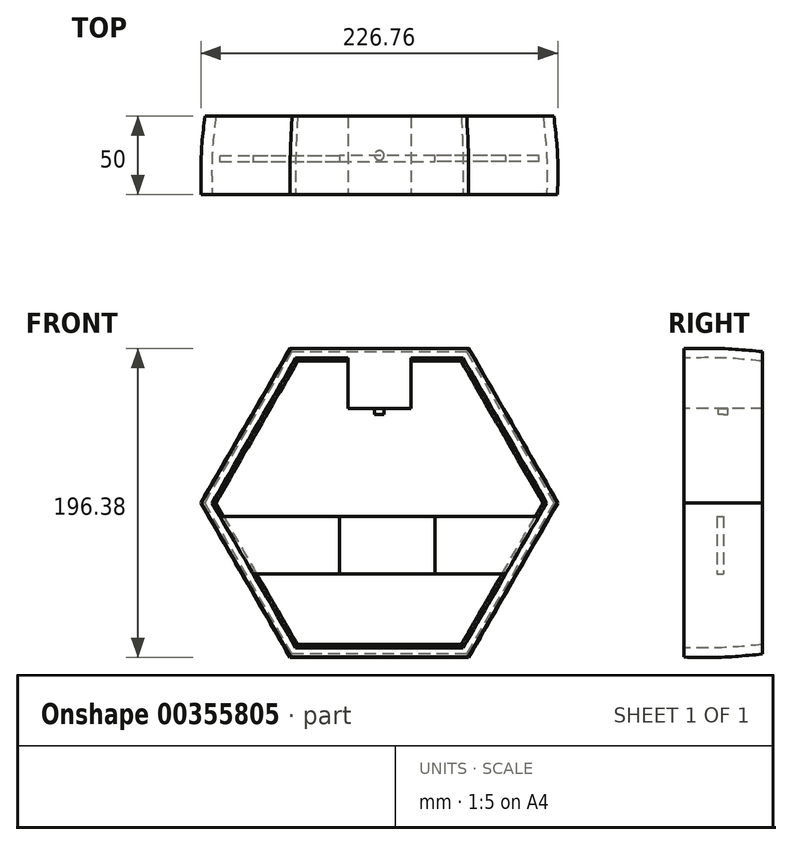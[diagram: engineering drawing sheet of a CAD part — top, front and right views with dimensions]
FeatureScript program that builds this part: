
annotation { "Feature Type Name" : "Feature", "Feature Type Description" : "" }
export const myFeature = defineFeature(function(context is Context, id is Id, definition is map)
    precondition{}
    {
        {
            var Q0;
            Q0=qCreatedBy(makeId("Front.planeOp"),FACE);
            var sketch = newSketch(context, id + "F0", { "sketchPlane" : qUnion([Q0])});
            skCircle(sketch, "E0.cCircle", {"center": v(0, 0) * mm, "radius": 98 * mm, "construction": true});
            skLineSegment(sketch, "E0.0", {"start": v(-56.58, 98) * mm, "end": v(56.58, 98) * mm});
            skLineSegment(sketch, "E0.1", {"start": v(56.58, 98) * mm, "end": v(113.16, 0) * mm});
            skLineSegment(sketch, "E0.2", {"start": v(113.16, 0) * mm, "end": v(56.58, -98) * mm});
            skLineSegment(sketch, "E0.3", {"start": v(56.58, -98) * mm, "end": v(-56.58, -98) * mm});
            skLineSegment(sketch, "E0.4", {"start": v(-56.58, -98) * mm, "end": v(-113.16, 0) * mm});
            skLineSegment(sketch, "E0.5", {"start": v(-113.16, 0) * mm, "end": v(-56.58, 98) * mm});
            skPoint(sketch, "E0.0.midPoint", {"position": v(0, 98) * mm});
            skSolve(sketch);
        }
        {
            var Q0;
            Q0=qCreatedBy(makeId("Front.planeOp"),FACE);
            cPlane(context, id + "F1", {"entities" : qUnion([Q0]), "cplaneType" : CPlaneType.OFFSET, "offset" : 25 * mm, "oppositeDirection" : true, "width" : 150 * mm, "height" : 150 * mm});
        }
        {
            var Q0;
            Q0=qCreatedBy(id+"F1.planeOp",FACE);
            var sketch = newSketch(context, id + "F2", { "sketchPlane" : qUnion([Q0])});
            skCircle(sketch, "E1.cCircle", {"center": v(0, 0) * mm, "radius": 96 * mm, "construction": true});
            skLineSegment(sketch, "E1.0", {"start": v(-55.43, 96) * mm, "end": v(55.43, 96) * mm});
            skLineSegment(sketch, "E1.1", {"start": v(55.43, 96) * mm, "end": v(110.85, 0) * mm});
            skLineSegment(sketch, "E1.2", {"start": v(110.85, 0) * mm, "end": v(55.43, -96) * mm});
            skLineSegment(sketch, "E1.3", {"start": v(55.43, -96) * mm, "end": v(-55.43, -96) * mm});
            skLineSegment(sketch, "E1.4", {"start": v(-55.43, -96) * mm, "end": v(-110.85, 0) * mm});
            skLineSegment(sketch, "E1.5", {"start": v(-110.85, 0) * mm, "end": v(-55.43, 96) * mm});
            skPoint(sketch, "E1.0.midPoint", {"position": v(0, 96) * mm});
            skSolve(sketch);
        }
        {
            var Q0;
            Q0=qCreatedBy(makeId("Front.planeOp"),FACE);
            cPlane(context, id + "F3", {"entities" : qUnion([Q0]), "cplaneType" : CPlaneType.OFFSET, "offset" : 25 * mm, "width" : 150 * mm, "height" : 150 * mm});
        }
        {
            var Q0;
            Q0=qCreatedBy(id+"F3.planeOp",FACE);
            var sketch = newSketch(context, id + "F4", { "sketchPlane" : qUnion([Q0])});
            skCircle(sketch, "E2.cCircle", {"center": v(0, 0) * mm, "radius": 98 * mm, "construction": true});
            skLineSegment(sketch, "E2.0", {"start": v(56.58, -98) * mm, "end": v(-56.58, -98) * mm});
            skLineSegment(sketch, "E2.1", {"start": v(-56.58, -98) * mm, "end": v(-113.16, 0) * mm});
            skLineSegment(sketch, "E2.2", {"start": v(-113.16, 0) * mm, "end": v(-56.58, 98) * mm});
            skLineSegment(sketch, "E2.3", {"start": v(-56.58, 98) * mm, "end": v(56.58, 98) * mm});
            skLineSegment(sketch, "E2.4", {"start": v(56.58, 98) * mm, "end": v(113.16, 0) * mm});
            skLineSegment(sketch, "E2.5", {"start": v(113.16, 0) * mm, "end": v(56.58, -98) * mm});
            skPoint(sketch, "E2.0.midPoint", {"position": v(0, -98) * mm});
            skSolve(sketch);
        }
        {
            var Q0;
            Q0=makeQuery(id+"F2.imprint","IMPRINT",FACE,{"disambiguationData":[TD([[makeQuery(id+"F2.imprint","IMPRINT",EDGE,{"derivedFrom":sQuery(id+"F2.wireOp",EDGE,"E1.0")}),-1.0]])]});
            var Q1;
            Q1=makeQuery(id+"F0.imprint","IMPRINT",FACE,{"disambiguationData":[TD([[makeQuery(id+"F0.imprint","IMPRINT",EDGE,{"derivedFrom":sQuery(id+"F0.wireOp",EDGE,"E0.0")}),-1.0]])]});
            var Q2;
            Q2=makeQuery(id+"F4.imprint","IMPRINT",FACE,{"disambiguationData":[TD([[makeQuery(id+"F4.imprint","IMPRINT",EDGE,{"derivedFrom":sQuery(id+"F4.wireOp",EDGE,"E2.0")}),-1.0]])]});
            loft(context, id + "F5", {"sheetProfilesArray" : [{ "sheetProfileEntities" : qUnion([Q0]) }, { "sheetProfileEntities" : qUnion([Q1]) }, { "sheetProfileEntities" : qUnion([Q2]) }]});
        }
        {
            var Q0;
            Q0=makeQuery(id+"F5.opLoft","CAP_FACE",FACE,{"disambiguationData":[OSD([makeQuery(id+"F2.imprint","IMPRINT",FACE,{"disambiguationData":[TD([[makeQuery(id+"F2.imprint","IMPRINT",EDGE,{"derivedFrom":sQuery(id+"F2.wireOp",EDGE,"E1.0")}),-1.0]])]})])],"isStart":true});
            var Q1;
            Q1=makeQuery(id+"F5.opLoft","CAP_FACE",FACE,{"disambiguationData":[OSD([makeQuery(id+"F4.imprint","IMPRINT",FACE,{"disambiguationData":[TD([[makeQuery(id+"F4.imprint","IMPRINT",EDGE,{"derivedFrom":sQuery(id+"F4.wireOp",EDGE,"E2.0")}),-1.0]])]})])],"isStart":true});
            shell(context, id + "F6", {"entities" : qUnion([Q0, Q1]), "thickness" : 6 * mm});
        }
        {
            var Q0;
            Q0=qCreatedBy(makeId("Top.planeOp"),FACE);
            cPlane(context, id + "F7", {"entities" : qUnion([Q0]), "cplaneType" : CPlaneType.OFFSET, "offset" : 45 * mm, "oppositeDirection" : true, "width" : 150 * mm, "height" : 150 * mm});
        }
        {
            var Q0;
            Q0=qCreatedBy(id+"F7.planeOp",FACE);
            var sketch = newSketch(context, id + "F8", { "sketchPlane" : qUnion([Q0])});
            skLineSegment(sketch, "E3", {"start": v(35.37, 0) * mm, "end": v(-25.32, 0) * mm});
            skLineSegment(sketch, "E4", {"start": v(-25.32, 0) * mm, "end": v(-25.32, -4) * mm});
            skLineSegment(sketch, "E5", {"start": v(-25.32, -4) * mm, "end": v(35.37, -4) * mm});
            skLineSegment(sketch, "E6", {"start": v(35.37, -4) * mm, "end": v(35.37, 0) * mm});
            skSolve(sketch);
        }
        {
            var Q0;
            Q0=qSketchRegion(id+"F8",true);
            extrude(context, id + "F9", {"entities" : qUnion([Q0]), "depth" : 36.5 * mm});
        }
        {
            var Q0;
            Q0=makeQuery(id+"F9.opExtrude","SWEPT_FACE",FACE,{"disambiguationData":[OSD([sQuery(id+"F8.wireOp",EDGE,"E4")])]});
            extrude(context, id + "F10", {"entities" : qUnion([Q0]), "endBound" : BoundingType.UP_TO_NEXT, "depth" : 25 * mm});
        }
        {
            var Q0;
            Q0=makeQuery(id+"F9.opExtrude","SWEPT_FACE",FACE,{"disambiguationData":[OSD([sQuery(id+"F8.wireOp",EDGE,"E6")])]});
            extrude(context, id + "F11", {"entities" : qUnion([Q0]), "endBound" : BoundingType.UP_TO_NEXT, "depth" : 25 * mm});
        }
        {
            var Q0;
            Q0=qCreatedBy(makeId("Top.planeOp"),FACE);
            cPlane(context, id + "F12", {"entities" : qUnion([Q0]), "cplaneType" : CPlaneType.OFFSET, "offset" : 60 * mm, "width" : 150 * mm, "height" : 150 * mm});
        }
        {
            var Q0;
            Q0=qCreatedBy(id+"F12.planeOp",FACE);
            var sketch = newSketch(context, id + "F13", { "sketchPlane" : qUnion([Q0])});
            skLineSegment(sketch, "E7.0", {"start": v(-20, 25) * mm, "end": v(20, 25) * mm});
            skLineSegment(sketch, "E7.1", {"start": v(-20, -25) * mm, "end": v(20, -25) * mm});
            skLineSegment(sketch, "E8.left", {"start": v(-20, 25) * mm, "end": v(-20, -25) * mm});
            skLineSegment(sketch, "E8.right", {"start": v(20, 25) * mm, "end": v(20, -25) * mm});
            skPoint(sketch, "E8.middle", {"position": v(0, 0) * mm});
            skPoint(sketch, "E9.orphan", {"position": v(55.43, 25) * mm});
            skPoint(sketch, "E10.orphan", {"position": v(56.58, -25) * mm});
            skPoint(sketch, "E11.orphan", {"position": v(-56.58, -25) * mm});
            skPoint(sketch, "E12.orphan", {"position": v(-55.43, 25) * mm});
            skSolve(sketch);
        }
        {
            var Q0;
            Q0=qSketchRegion(id+"F13",true);
            extrude(context, id + "F14", {"entities" : qUnion([Q0]), "operationType" : NewBodyOperationType.ADD, "endBound" : BoundingType.UP_TO_NEXT, "depth" : 25 * mm});
        }
        {
            var Q0;
            Q0=makeQuery(id+"F14.opExtrude","CAP_FACE",FACE,{"disambiguationData":[OSD([sQuery(id+"F13.wireOp",EDGE,"E7.0"),sQuery(id+"F13.wireOp",EDGE,"E7.1"),sQuery(id+"F13.wireOp",EDGE,"E8.left"),sQuery(id+"F13.wireOp",EDGE,"E8.right")])],"isStart":true});
            var sketch = newSketch(context, id + "F15", { "sketchPlane" : qUnion([Q0])});
            skCircle(sketch, "E13", {"center": v(0, 0) * mm, "radius": 3 * mm});
            skSolve(sketch);
        }
        {
            var Q0;
            Q0=qSketchRegion(id+"F15",true);
            extrude(context, id + "F16", {"entities" : qUnion([Q0]), "operationType" : NewBodyOperationType.ADD, "depth" : 4 * mm});
        }
    });
